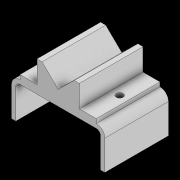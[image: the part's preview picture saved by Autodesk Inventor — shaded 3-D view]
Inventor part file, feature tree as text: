
AUTODESK INVENTOR PART (.ipt)
format: ipt  version: 2021 (Build 250183000, 183)  size: 140,800 bytes
history: native  units: mm
features: extrude x2, sketch x2
ambient origin geometry x8: Origin, YZ Plane, XZ Plane, XY Plane, X Axis, Y Axis, Z Axis, Center Point
bodies: Solid1 (feature_tree)
feature tree (4):
  extrude  "Extrusion1"  Depth=100.0mm
  extrude  "Extrusion4"  Depth=10.0mm
  sketch  "Sketch1"  dims[d0=100.0mm d1=100.0mm]
  sketch  "Sketch4"  dims[d2=80.0mm d4=10.0mm d5=10.0mm d6=150.0mm d7=0.0mm d24=10.0mm d25=50.0mm d26=50.0mm d31=12.0mm d32=12.0mm d33=50.0mm d34=75.0mm d35=15.0mm d36=75.0mm d37=15.0mm d38=20.0mm d39=20.0mm d40=52.0mm d41=52.0mm d42=16.0mm d43=20.0mm d44=20.0mm d45=75.0mm d46=75.0mm d47=50.0mm d48=0.0mm]
